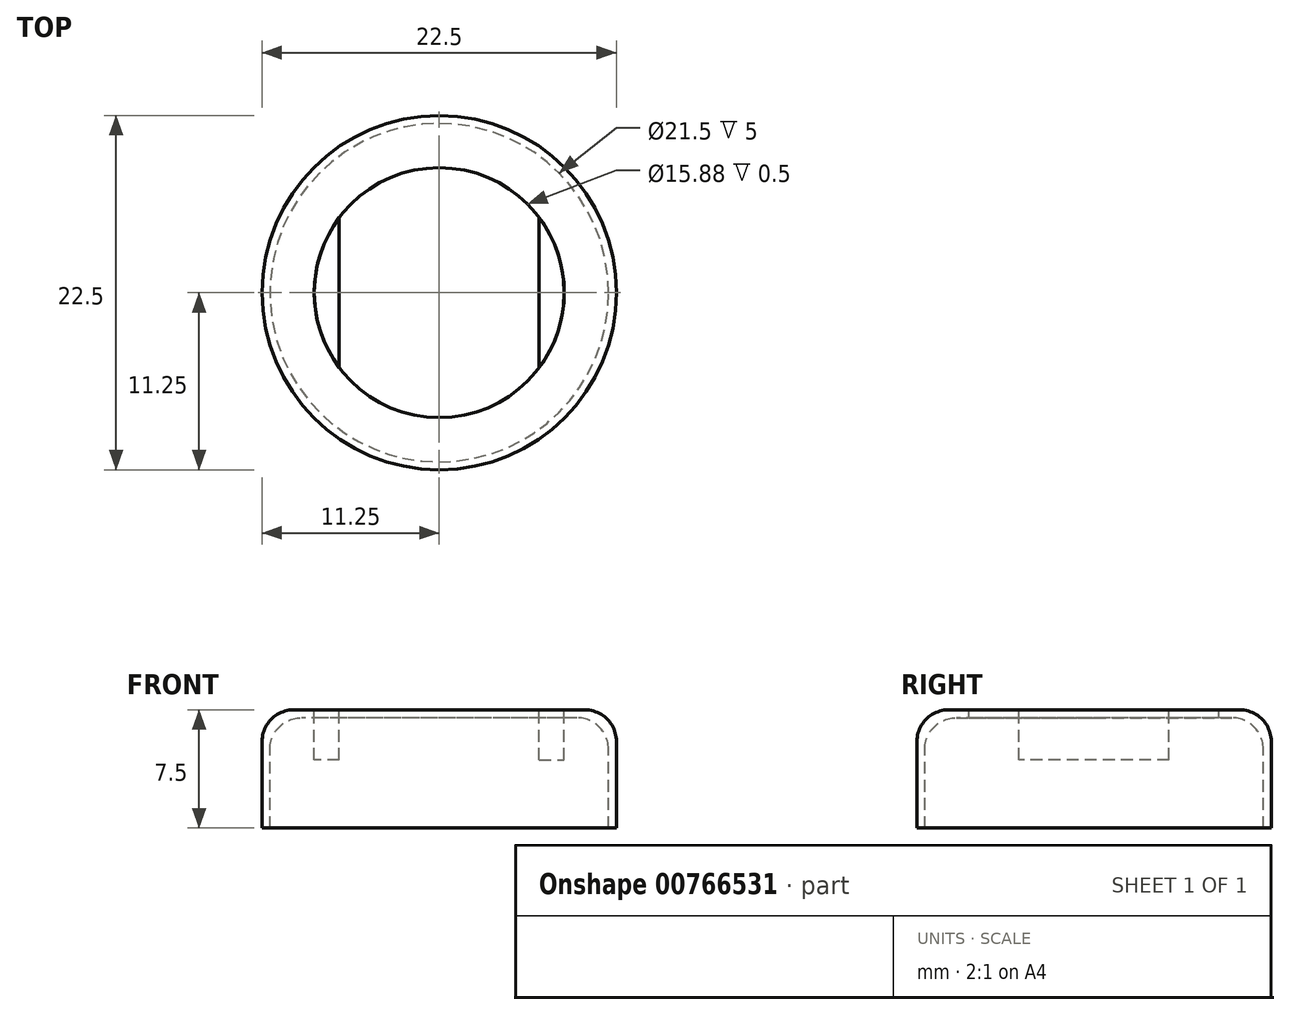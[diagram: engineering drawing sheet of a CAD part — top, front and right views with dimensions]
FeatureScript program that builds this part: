
annotation { "Feature Type Name" : "Feature", "Feature Type Description" : "" }
export const myFeature = defineFeature(function(context is Context, id is Id, definition is map)
    precondition{}
    {
        {
            var Q0;
            Q0=qCreatedBy(makeId("Top.planeOp"),FACE);
            var sketch = newSketch(context, id + "F0", { "sketchPlane" : qUnion([Q0])});
            skCircle(sketch, "E0", {"center": v(0, 0) * mm, "radius": 7.94 * mm});
            skCircle(sketch, "E1", {"center": v(0, 0) * mm, "radius": 12 * mm});
            skPoint(sketch, "E2", {"position": v(-7.94, 0) * mm});
            skPoint(sketch, "E3", {"position": v(7.94, 0) * mm});
            skPoint(sketch, "E4", {"position": v(12, 0) * mm});
            skPoint(sketch, "E5", {"position": v(-12, 0) * mm});
            skPoint(sketch, "E6.MirrorCS.end.orphan", {"position": v(6.35, -4.76) * mm});
            skPoint(sketch, "E6.MirrorCS.start.orphan", {"position": v(6.35, 0) * mm});
            skPoint(sketch, "E7.MirrorCS.end.orphan", {"position": v(6.35, 4.76) * mm});
            skPoint(sketch, "E8.end.orphan", {"position": v(-6.35, 4.76) * mm});
            skPoint(sketch, "E9.end.orphan", {"position": v(-6.35, -4.76) * mm});
            skPoint(sketch, "E9.start.orphan", {"position": v(-6.35, 0) * mm});
            skLineSegment(sketch, "E10", {"start": v(-6.35, 4.76) * mm, "end": v(-6.35, -4.76) * mm});
            skLineSegment(sketch, "E11", {"start": v(6.35, 4.76) * mm, "end": v(6.35, -4.76) * mm});
            skSolve(sketch);
        }
        {
            var Q0;
            Q0=qCreatedBy(makeId("Front.planeOp"),FACE);
            var sketch = newSketch(context, id + "F1", { "sketchPlane" : qUnion([Q0])});
            skLineSegment(sketch, "E12", {"start": v(7.94, 0) * mm, "end": v(7.94, -0.5) * mm});
            skLineSegment(sketch, "E13", {"start": v(11.25, -7.5) * mm, "end": v(10.75, -7.5) * mm});
            skLineSegment(sketch, "E14", {"start": v(0, 0) * mm, "end": v(0, -7.5) * mm});
            skLineSegment(sketch, "E15", {"start": v(11.25, -7.5) * mm, "end": v(11.25, -2) * mm});
            skLineSegment(sketch, "E16", {"start": v(9.25, 0) * mm, "end": v(7.94, 0) * mm});
            skLineSegment(sketch, "E17", {"start": v(7.94, -0.5) * mm, "end": v(8.75, -0.5) * mm});
            skLineSegment(sketch, "E18", {"start": v(10.75, -7.5) * mm, "end": v(10.75, -2.5) * mm});
            skPoint(sketch, "E19.orphan", {"position": v(11.25, -0.5) * mm});
            skPoint(sketch, "E20.visualSharp", {"position": v(10.75, -0.5) * mm});
            skArc(sketch, "E20.filletArc", {"start": v(10.75, -2.5) * mm, "mid": v(10.16, -1.09) * mm, "end": v(8.75, -0.5) * mm});
            skPoint(sketch, "E21.visualSharp", {"position": v(11.25, 0) * mm});
            skArc(sketch, "E21.filletArc", {"start": v(11.25, -2) * mm, "mid": v(10.66, -0.59) * mm, "end": v(9.25, 0) * mm});
            skSolve(sketch);
        }
        {
            var Q0;
            {var subQ0=sQuery(id+"F0.wireOp",EDGE,"E10");Q0=makeQuery(id+"F0.imprint","IMPRINT",FACE,{"disambiguationData":[TD([[makeQuery(id+"F0.imprint","IMPRINT",EDGE,{"derivedFrom":subQ0}),-1.0]])]});}
            extrude(context, id + "F2", {"entities" : qUnion([Q0]), "oppositeDirection" : true, "depth" : 3.17 * mm, "offsetDistance" : 25.4 * mm});
        }
        {
            var Q0;
            Q0=makeQuery(id+"F2.opExtrude","SWEPT_BODY",BODY,{"disambiguationData":[OSD([sQuery(id+"F0.wireOp",EDGE,"E0"),sQuery(id+"F0.wireOp",EDGE,"E10")])]});
            var Q1;
            Q1=qCreatedBy(makeId("Right.planeOp"),FACE);
            mirror(context, id + "F3", {"operationType" : NewBodyOperationType.ADD, "entities" : qUnion([Q0]), "mirrorPlane" : qUnion([Q1])});
        }
        {
            var Q0;
            Q0=makeQuery(id+"F1.imprint","IMPRINT",FACE,{"disambiguationData":[TD([[makeQuery(id+"F1.imprint","IMPRINT",EDGE,{"derivedFrom":sQuery(id+"F1.wireOp",EDGE,"E12")}),1.0]])]});
            var Q1;
            Q1=sQuery(id+"F1.wireOp",EDGE,"E14");
            revolve(context, id + "F4", {"surfaceOperationType" : NewSurfaceOperationType.NEW, "entities" : qUnion([Q0]), "axis" : qUnion([Q1]), "revolveType" : RevolveType.FULL});
        }
    });
